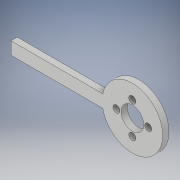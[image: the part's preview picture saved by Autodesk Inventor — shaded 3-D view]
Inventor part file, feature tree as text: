
AUTODESK INVENTOR PART (.ipt)
format: ipt  version: 2017 (Build 210142000, 142)  size: 139,776 bytes
history: native  units: in
note: dims shown in document units (in); Inventor stores cm internally (conversion verified against a paired STEP export)
features: sketch x5, extrude x5, plane x1
ambient origin geometry x8: Origin, YZ Plane, XZ Plane, XY Plane, X Axis, Y Axis, Z Axis, Center Point
bodies: Solid1 (feature_tree)
feature tree (11):
  sketch  "Sketch1"  dims[d0=1.2in d1=0.125in d2=0.0in]
  extrude  "Extrusion1"  Depth=0.125in TaperAngle=0.0deg
  sketch  "Sketch2"  dims[d3=0.125in d4=0.125in]
  plane  "Work Plane1"
  extrude  "Extrusion2"  Depth=0.125in
  extrude  "Extrusion3"  Depth=0.25in TaperAngle=0.0deg
  extrude  "Extrusion4"  Depth=0.315in
  extrude  "Extrusion5"  Depth=0.315in
  sketch  "Sketch3"  dims[d6=0.25in d7=1.8045in d8=0.0in]
  sketch  "Sketch4"  dims[d9=0.5in d10=0.0in d11=0.315in]
  sketch  "Sketch5"  dims[d12=0.315in d13=0.315in d14=0.315in d15=0.138in d16=0.138in d17=0.138in d18=0.138in d19=0.5in d20=0.0in d21=0.45in d22=0.5in d23=0.0in]
